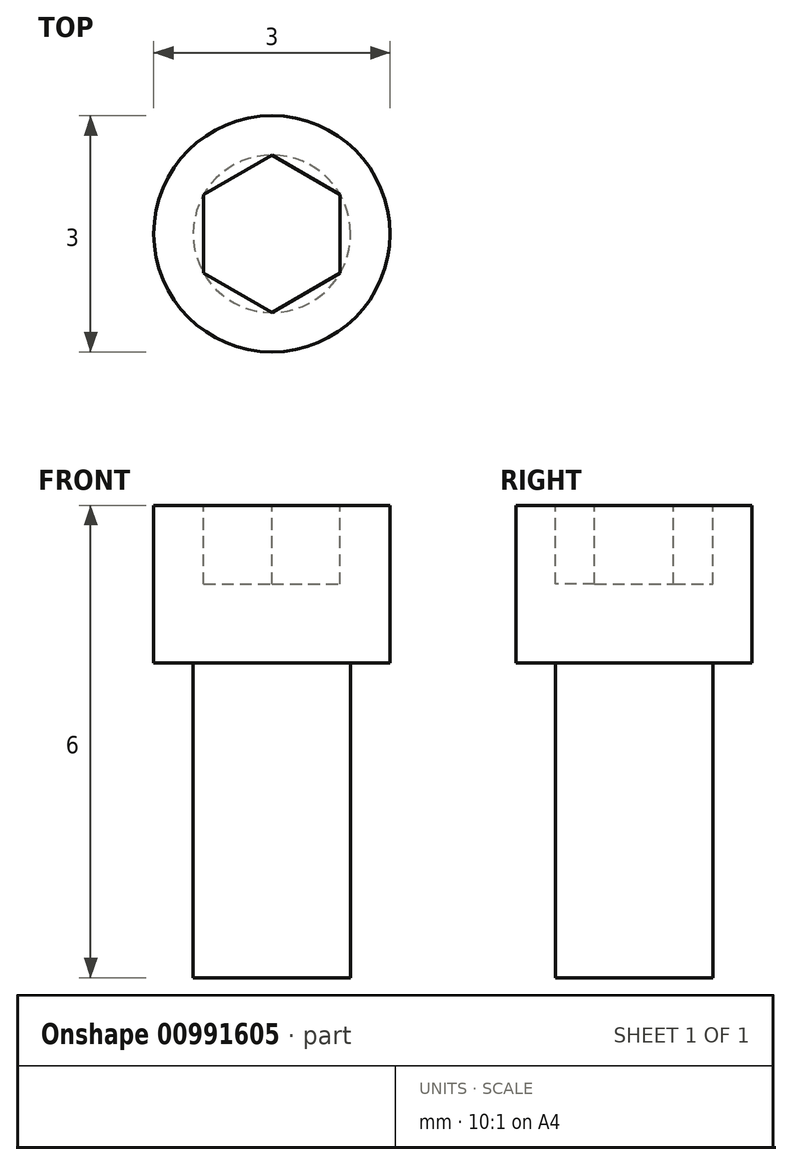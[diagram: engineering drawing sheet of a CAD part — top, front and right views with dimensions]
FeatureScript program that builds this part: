
annotation { "Feature Type Name" : "Feature", "Feature Type Description" : "" }
export const myFeature = defineFeature(function(context is Context, id is Id, definition is map)
    precondition{}
    {
        {
            var Q0;
            Q0=qCreatedBy(makeId("Top.planeOp"),FACE);
            var sketch = newSketch(context, id + "F0", { "sketchPlane" : qUnion([Q0])});
            skCircle(sketch, "E0", {"center": v(0, 0) * mm, "radius": 1 * mm});
            skSolve(sketch);
        }
        {
            var Q0;
            Q0=qSketchRegion(id+"F0",true);
            extrude(context, id + "F1", {"entities" : qUnion([Q0]), "depth" : 4 * mm, "offsetDistance" : 25 * mm});
        }
        {
            var Q0;
            Q0=makeQuery(id+"F1.opExtrude","CAP_FACE",FACE,{"disambiguationData":[OSD([sQuery(id+"F0.wireOp",EDGE,"E0")])],"isStart":false});
            var sketch = newSketch(context, id + "F2", { "sketchPlane" : qUnion([Q0])});
            skCircle(sketch, "E1", {"center": v(0, 0) * mm, "radius": 1.5 * mm});
            skSolve(sketch);
        }
        {
            var Q0;
            Q0=qSketchRegion(id+"F2",true);
            extrude(context, id + "F3", {"entities" : qUnion([Q0]), "operationType" : NewBodyOperationType.ADD, "depth" : 2 * mm, "offsetDistance" : 25 * mm});
        }
        {
            var Q0;
            Q0=makeQuery(id+"F3.opExtrude","CAP_FACE",FACE,{"disambiguationData":[OSD([sQuery(id+"F2.wireOp",EDGE,"E1")])],"isStart":false});
            var sketch = newSketch(context, id + "F4", { "sketchPlane" : qUnion([Q0])});
            skLineSegment(sketch, "E2", {"start": v(0, 1.5) * mm, "end": v(0, -1.5) * mm, "construction": true});
            skLineSegment(sketch, "E3", {"start": v(-1.5, 0) * mm, "end": v(1.5, 0) * mm, "construction": true});
            skLineSegment(sketch, "E4", {"start": v(0, -1) * mm, "end": v(0.87, -0.5) * mm});
            skLineSegment(sketch, "E5", {"start": v(0.87, -0.5) * mm, "end": v(0.87, 0.5) * mm});
            skLineSegment(sketch, "E6", {"start": v(0.87, 0.5) * mm, "end": v(0, 1) * mm});
            skLineSegment(sketch, "E7", {"start": v(0, 1) * mm, "end": v(-0.87, 0.5) * mm});
            skLineSegment(sketch, "E8", {"start": v(-0.87, 0.5) * mm, "end": v(-0.87, -0.5) * mm});
            skLineSegment(sketch, "E9", {"start": v(-0.87, -0.5) * mm, "end": v(0, -1) * mm});
            skSolve(sketch);
        }
        {
            var Q0;
            Q0=qSketchRegion(id+"F4",true);
            extrude(context, id + "F5", {"entities" : qUnion([Q0]), "operationType" : NewBodyOperationType.REMOVE, "oppositeDirection" : true, "depth" : 1 * mm, "offsetDistance" : 25 * mm});
        }
    });
